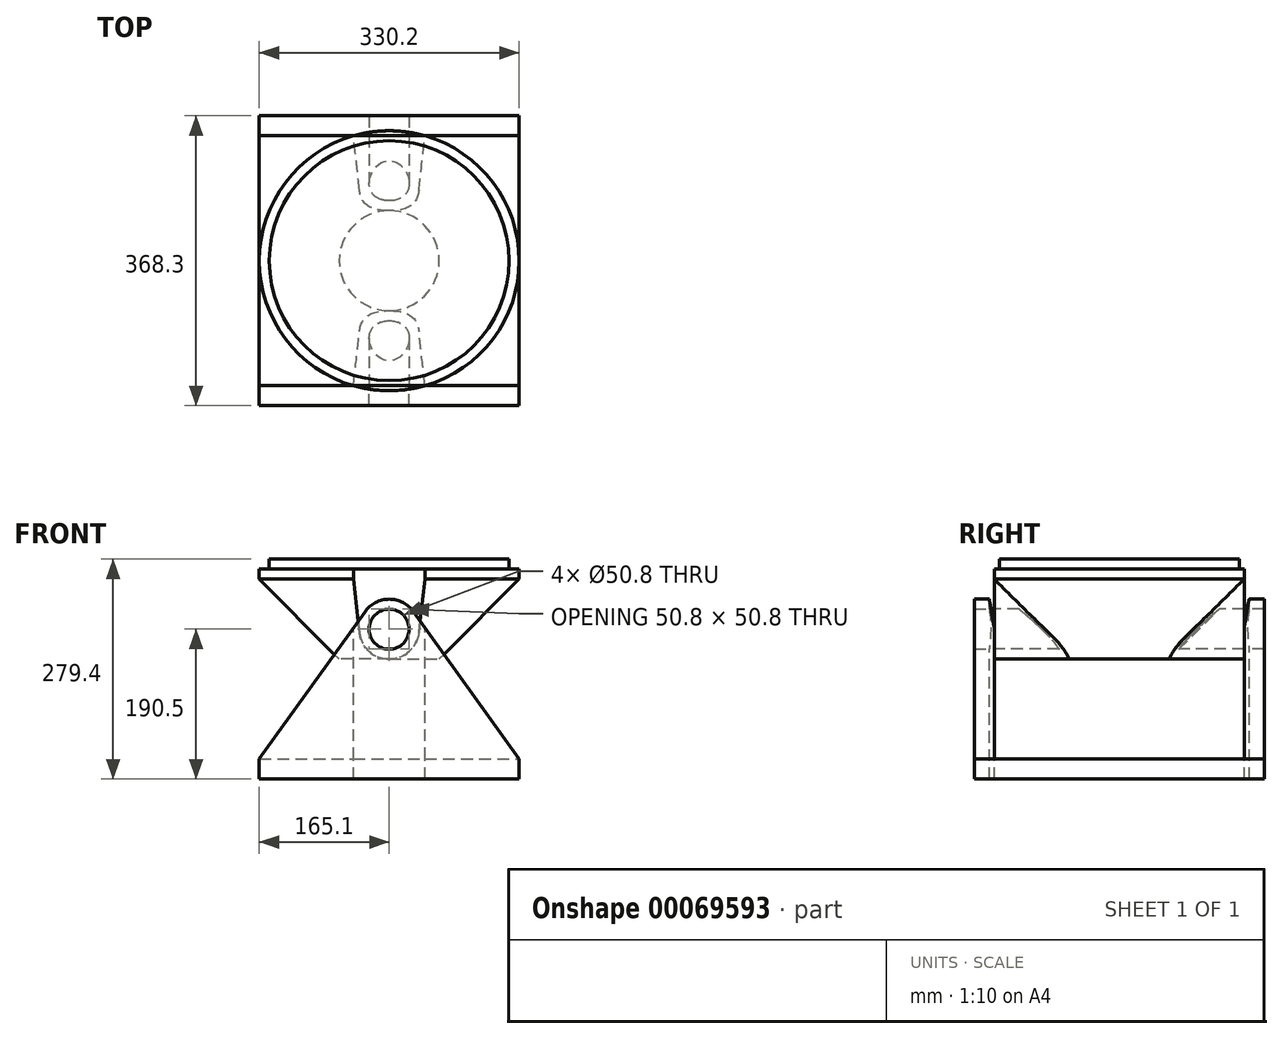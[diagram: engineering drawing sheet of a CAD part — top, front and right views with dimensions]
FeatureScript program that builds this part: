
annotation { "Feature Type Name" : "Feature", "Feature Type Description" : "" }
export const myFeature = defineFeature(function(context is Context, id is Id, definition is map)
    precondition{}
    {
        {
            var Q0;
            Q0=qCreatedBy(makeId("Top.planeOp"),FACE);
            var sketch = newSketch(context, id + "F0", { "sketchPlane" : qUnion([Q0])});
            skLineSegment(sketch, "E0.rect.bottom", {"start": v(-165.1, 158.75) * mm, "end": v(165.1, 158.75) * mm});
            skLineSegment(sketch, "E0.rect.top", {"start": v(-165.1, -158.75) * mm, "end": v(165.1, -158.75) * mm});
            skLineSegment(sketch, "E0.rect.left", {"start": v(-165.1, 158.75) * mm, "end": v(-165.1, -158.75) * mm});
            skLineSegment(sketch, "E0.rect.right", {"start": v(165.1, 158.75) * mm, "end": v(165.1, -158.75) * mm});
            skPoint(sketch, "E0.rect.middle", {"position": v(0, 0) * mm});
            skLineSegment(sketch, "E1", {"start": v(-165.1, 0) * mm, "end": v(165.1, 0) * mm, "construction": true});
            skSolve(sketch);
        }
        {
            var Q0;
            Q0=qSketchRegion(id+"F0",true);
            extrude(context, id + "F1", {"entities" : qUnion([Q0]), "depth" : 25.4 * mm});
        }
        {
            var Q0;
            Q0=makeQuery(id+"F1.opExtrude","SWEPT_FACE",FACE,{"disambiguationData":[OSD([sQuery(id+"F0.wireOp",EDGE,"E0.rect.top")])]});
            var sketch = newSketch(context, id + "F2", { "sketchPlane" : qUnion([Q0])});
            skLineSegment(sketch, "E2.bottom", {"start": v(-165.1, 0) * mm, "end": v(165.1, 0) * mm});
            skLineSegment(sketch, "E2.top", {"start": v(-165.1, 25.4) * mm, "end": v(165.1, 25.4) * mm});
            skLineSegment(sketch, "E2.left", {"start": v(-165.1, 0) * mm, "end": v(-165.1, 25.4) * mm});
            skLineSegment(sketch, "E2.right", {"start": v(165.1, 0) * mm, "end": v(165.1, 25.4) * mm});
            skCircle(sketch, "E3", {"center": v(0, 190.5) * mm, "radius": 25.4 * mm});
            skPoint(sketch, "E3.centerSnap0", {"position": v(0, 25.4) * mm});
            skCircle(sketch, "E4", {"center": v(0, 190.5) * mm, "radius": 38.1 * mm});
            skLineSegment(sketch, "E5", {"start": v(-165.1, 25.4) * mm, "end": v(-30.98, 212.68) * mm});
            skLineSegment(sketch, "E6", {"start": v(165.1, 25.4) * mm, "end": v(30.98, 212.68) * mm});
            skSolve(sketch);
        }
        {
            var Q0;
            Q0=makeQuery(id+"F2.imprint","IMPRINT",FACE,{"disambiguationData":[TD([[makeQuery(id+"F2.imprint","IMPRINT",EDGE,{"derivedFrom":sQuery(id+"F2.wireOp",EDGE,"E2.bottom")}),1.0]])]});
            var Q1;
            Q1=makeQuery(id+"F2.imprint","IMPRINT",FACE,{"disambiguationData":[TD([[makeQuery(id+"F2.imprint","IMPRINT",EDGE,{"derivedFrom":sQuery(id+"F2.wireOp",EDGE,"E2.top")}),1.0]])]});
            var Q2;
            Q2=makeQuery(id+"F2.imprint","IMPRINT",FACE,{"disambiguationData":[TD([[makeQuery(id+"F2.imprint","IMPRINT",EDGE,{"derivedFrom":sQuery(id+"F2.wireOp",EDGE,"E3")}),-1.0]])]});
            extrude(context, id + "F3", {"entities" : qUnion([Q0, Q1, Q2]), "depth" : 25.4 * mm});
        }
        {
            var Q0;
            Q0=makeQuery(id+"F3.opExtrude","SWEPT_BODY",BODY,{"disambiguationData":[OSD([sQuery(id+"F2.wireOp",EDGE,"E2.bottom"),sQuery(id+"F2.wireOp",EDGE,"E2.left"),sQuery(id+"F2.wireOp",EDGE,"E2.right"),sQuery(id+"F2.wireOp",EDGE,"E3"),sQuery(id+"F2.wireOp",EDGE,"E4"),sQuery(id+"F2.wireOp",EDGE,"E5"),sQuery(id+"F2.wireOp",EDGE,"E6")])]});
            var Q1;
            Q1=qCreatedBy(makeId("Front.planeOp"),FACE);
            mirror(context, id + "F4", {"operationType" : NewBodyOperationType.ADD, "entities" : qUnion([Q0]), "mirrorPlane" : qUnion([Q1])});
        }
        {
            var Q0;
            Q0=qCreatedBy(makeId("Top.planeOp"),FACE);
            cPlane(context, id + "F5", {"entities" : qUnion([Q0]), "cplaneType" : CPlaneType.OFFSET, "offset" : 266.7 * mm, "width" : 152.4 * mm, "height" : 152.4 * mm});
        }
        {
            var Q0;
            Q0=qCreatedBy(id+"F5.planeOp",FACE);
            var sketch = newSketch(context, id + "F6", { "sketchPlane" : qUnion([Q0])});
            skCircle(sketch, "E7", {"center": v(0, 0) * mm, "radius": 165.1 * mm});
            skLineSegment(sketch, "E8", {"start": v(210.97, 0) * mm, "end": v(-227.74, 0) * mm, "construction": true});
            skLineSegment(sketch, "E9", {"start": v(-45.35, 158.75) * mm, "end": v(45.35, 158.75) * mm});
            skLineSegment(sketch, "E10", {"start": v(-45.35, -158.75) * mm, "end": v(45.35, -158.75) * mm});
            skSolve(sketch);
        }
        {
            var Q0;
            {var subQ0=sQuery(id+"F6.wireOp",EDGE,"E9");Q0=makeQuery(id+"F6.imprint","IMPRINT",FACE,{"disambiguationData":[TD([[makeQuery(id+"F6.imprint","IMPRINT",EDGE,{"derivedFrom":subQ0}),-1.0]])]});}
            var Q1;
            {var subQ0=sQuery(id+"F6.wireOp",EDGE,"E10");Q1=makeQuery(id+"F6.imprint","IMPRINT",FACE,{"disambiguationData":[TD([[makeQuery(id+"F6.imprint","IMPRINT",EDGE,{"derivedFrom":subQ0}),-1.0]])]});}
            var Q2;
            {var subQ0=sQuery(id+"F6.wireOp",EDGE,"E9");Q2=makeQuery(id+"F6.imprint","IMPRINT",FACE,{"disambiguationData":[TD([[makeQuery(id+"F6.imprint","IMPRINT",EDGE,{"derivedFrom":subQ0}),1.0]])]});}
            extrude(context, id + "F7", {"entities" : qUnion([Q0, Q1, Q2]), "oppositeDirection" : true, "depth" : 12.7 * mm});
        }
        {
            var Q0;
            Q0=makeQuery(id+"F7.opExtrude","CAP_FACE",FACE,{"disambiguationData":[OSD([sQuery(id+"F6.wireOp",EDGE,"E7")])],"isStart":false});
            extrude(context, id + "F8", {"entities" : qUnion([Q0]), "operationType" : NewBodyOperationType.ADD, "depth" : 101.6 * mm, "hasDraft" : true, "draftAngle" : 45 * degree, "draftPullDirection" : true});
        }
        {
            var Q0;
            {var subQ0=sQuery(id+"F6.wireOp",EDGE,"E9");Q0=makeQuery(id+"F6.imprint","IMPRINT",FACE,{"disambiguationData":[TD([[makeQuery(id+"F6.imprint","IMPRINT",EDGE,{"derivedFrom":subQ0}),1.0]])]});}
            var Q1;
            {var subQ0=sQuery(id+"F6.wireOp",EDGE,"E10");Q1=makeQuery(id+"F6.imprint","IMPRINT",FACE,{"disambiguationData":[TD([[makeQuery(id+"F6.imprint","IMPRINT",EDGE,{"derivedFrom":subQ0}),-1.0]])]});}
            extrude(context, id + "F9", {"entities" : qUnion([Q0, Q1]), "operationType" : NewBodyOperationType.REMOVE, "endBound" : BoundingType.THROUGH_ALL, "oppositeDirection" : true, "depth" : 25.4 * mm});
        }
        {
            var Q0;
            Q0=makeQuery(id+"F9.boolean.opBoolean","COPY",FACE,{"derivedFrom":makeQuery(id+"F9.opExtrude","SWEPT_FACE",FACE,{"disambiguationData":[OSD([sQuery(id+"F6.wireOp",EDGE,"E10")])]})});
            var sketch = newSketch(context, id + "F10", { "sketchPlane" : qUnion([Q0])});
            skLineSegment(sketch, "E11.0", {"start": v(-45.35, 266.7) * mm, "end": v(45.35, 266.7) * mm});
            skCircle(sketch, "E12", {"center": v(0, 190.5) * mm, "radius": 38.1 * mm});
            skLineSegment(sketch, "E13.0", {"start": v(-45.35, 254) * mm, "end": v(-45.35, 266.7) * mm});
            skLineSegment(sketch, "E14.0", {"start": v(45.35, 254) * mm, "end": v(45.35, 266.7) * mm});
            skLineSegment(sketch, "E15", {"start": v(-45.35, 254) * mm, "end": v(-37.87, 186.32) * mm});
            skLineSegment(sketch, "E16", {"start": v(45.35, 254) * mm, "end": v(37.87, 186.32) * mm});
            skCircle(sketch, "E17", {"center": v(0, 190.5) * mm, "radius": 25.4 * mm});
            skSolve(sketch);
        }
        {
            var Q0;
            Q0=makeQuery(id+"F10.imprint","IMPRINT",FACE,{"disambiguationData":[TD([[makeQuery(id+"F10.imprint","IMPRINT",EDGE,{"derivedFrom":sQuery(id+"F10.wireOp",EDGE,"E17")}),-1.0]])]});
            var Q1;
            {var subQ0=sQuery(id+"F10.wireOp",EDGE,"E15");Q1=makeQuery(id+"F10.imprint","IMPRINT",FACE,{"disambiguationData":[TD([[makeQuery(id+"F10.imprint","IMPRINT",EDGE,{"derivedFrom":subQ0}),1.0]])]});}
            var Q2;
            Q2=makeQuery(id+"F9.boolean.opBoolean","COPY",FACE,{"derivedFrom":makeQuery(id+"F9.opExtrude","SWEPT_FACE",FACE,{"disambiguationData":[OSD([sQuery(id+"F6.wireOp",EDGE,"E9")])]})});
            extrude(context, id + "F11", {"entities" : qUnion([Q0, Q1]), "operationType" : NewBodyOperationType.ADD, "endBound" : BoundingType.UP_TO_SURFACE, "oppositeDirection" : true, "endBoundEntityFace" : qUnion([Q2]), "depth" : 25.4 * mm});
        }
        {
            var Q0;
            {var subQ0=sQuery(id+"F6.wireOp",EDGE,"E9");Q0=makeQuery(id+"F6.imprint","IMPRINT",FACE,{"disambiguationData":[TD([[makeQuery(id+"F6.imprint","IMPRINT",EDGE,{"derivedFrom":subQ0}),-1.0]])]});}
            var sketch = newSketch(context, id + "F12", { "sketchPlane" : qUnion([Q0])});
            skCircle(sketch, "E18", {"center": v(0, 0) * mm, "radius": 152.4 * mm});
            skSolve(sketch);
        }
        {
            var Q0;
            Q0=qSketchRegion(id+"F12",true);
            extrude(context, id + "F13", {"entities" : qUnion([Q0]), "depth" : 12.7 * mm});
        }
    });
